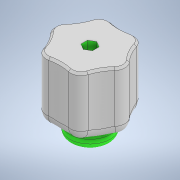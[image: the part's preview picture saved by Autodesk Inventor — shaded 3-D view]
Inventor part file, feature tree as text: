
AUTODESK INVENTOR PART (.ipt)
format: ipt  version: 2022 (Build 260153000, 153)  size: 517,120 bytes
history: native  units: mm
features: extrude x3, fillet x3, sketch x2, chamfer x1
ambient origin geometry x8: Origin, YZ Plane, XZ Plane, XY Plane, X Axis, Y Axis, Z Axis, Center Point
bodies: Solid1 (feature_tree)
feature tree (9):
  extrude  "Extrusion1"  Depth=30.0mm TaperAngle=0.0deg
  extrude  "Extrusion2"  Depth=5.25mm
  extrude  "Extrusion3"  Depth=5.25mm TaperAngle=0.0deg
  fillet  "Fillet1"  Radius=10.0mm
  fillet  "Fillet2"  Radius=20.0mm
  fillet  "Fillet3"  Radius=8.0mm
  chamfer  "Chamfer2"  Distance=3.0mm
  sketch  "Sketch2"  dims[d0=3.2mm d1=30.0mm d2=0.0mm]
  sketch  "Sketch3"  dims[d3=40.0mm d4=5.7mm d5=5.0mm d6=0.0mm d7=10.0mm d8=20.0mm d9=8.0mm d10=0.0mm d11=3.0mm d15=60.0mm d17=360.0deg d19=20.0mm d20=5.25mm d21=5.25mm d22=1.0mm d23=2.0mm d24=45.0deg]
